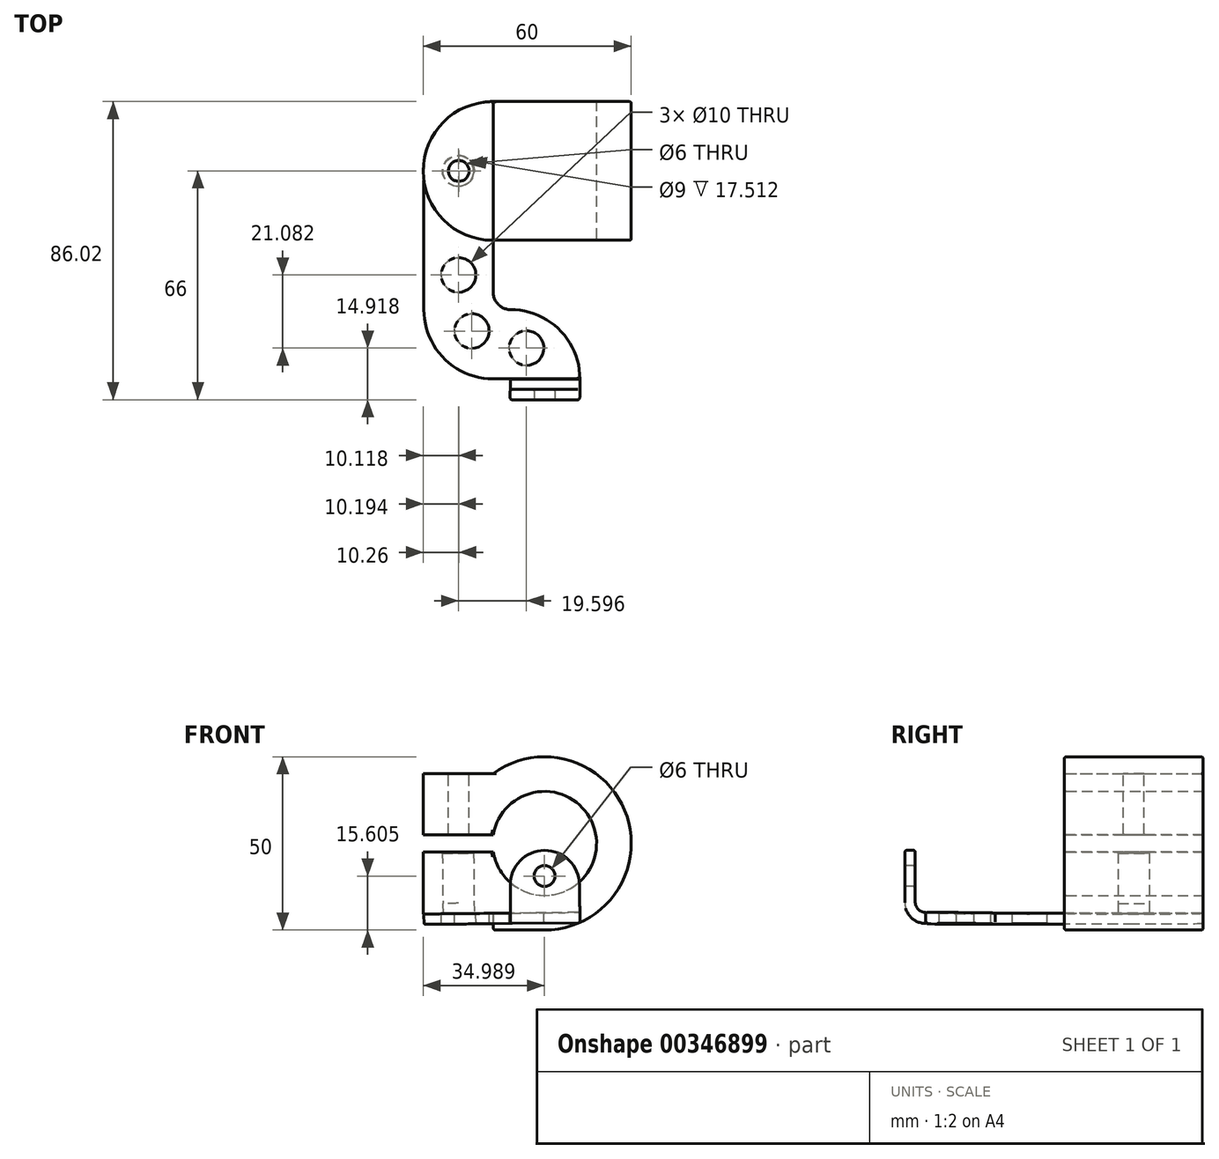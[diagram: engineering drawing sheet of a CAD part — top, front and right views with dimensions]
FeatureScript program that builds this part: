
annotation { "Feature Type Name" : "Feature", "Feature Type Description" : "" }
export const myFeature = defineFeature(function(context is Context, id is Id, definition is map)
    precondition{}
    {
        {
            var Q0;
            Q0=qCreatedBy(makeId("Front.planeOp"),FACE);
            var sketch = newSketch(context, id + "F0", { "sketchPlane" : qUnion([Q0])});
            skLineSegment(sketch, "E0.right", {"start": v(30, 0.21) * mm, "end": v(30, 0.21) * mm});
            skArc(sketch, "E1", {"start": v(-9.8, -2.5) * mm, "mid": v(20, 0) * mm, "end": v(-9.8, 2.5) * mm});
            skArc(sketch, "E2.filletArc", {"start": v(30, 0.21) * mm, "mid": v(16.2, 22.35) * mm, "end": v(-9.8, 20.16) * mm});
            skArc(sketch, "E3.filletArc", {"start": v(5, -25) * mm, "mid": v(22.75, -17.6) * mm, "end": v(30, 0.21) * mm});
            skLineSegment(sketch, "E4", {"start": v(-30, -2.5) * mm, "end": v(-9.8, -2.5) * mm});
            skLineSegment(sketch, "E5", {"start": v(-30, 2.5) * mm, "end": v(-9.8, 2.5) * mm});
            skLineSegment(sketch, "E6", {"start": v(-9.8, 20.16) * mm, "end": v(-30, 20.16) * mm});
            skLineSegment(sketch, "E7", {"start": v(-30, 20.16) * mm, "end": v(-30, 2.5) * mm});
            skLineSegment(sketch, "E8", {"start": v(-9.8, -20.16) * mm, "end": v(-9.74, -25) * mm});
            skLineSegment(sketch, "E9", {"start": v(-9.8, -20.16) * mm, "end": v(-30, -20.37) * mm});
            skLineSegment(sketch, "E10", {"start": v(-30, -2.5) * mm, "end": v(-30, -20.37) * mm});
            skLineSegment(sketch, "E11", {"start": v(-9.74, -25) * mm, "end": v(5, -25) * mm});
            skSolve(sketch);
        }
        {
            var Q0;
            Q0 = qSketchRegion(id + "F0", true);
            extrude(context, id + "F1", {"entities" : qUnion([Q0]), "endBound" : BoundingType.SYMMETRIC, "depth" : 40 * mm});
        }
        {
            var Q0;
            Q0=makeQuery(id+"F1.opExtrude","SWEPT_FACE",FACE,{"disambiguationData":[OSD([sQuery(id+"F0.wireOp",EDGE,"E6")])]});
            var sketch = newSketch(context, id + "F2", { "sketchPlane" : qUnion([Q0])});
            skCircle(sketch, "E12", {"center": v(-19.74, 0) * mm, "radius": 3 * mm});
            skSolve(sketch);
        }
        {
            var Q0;
            Q0 = qSketchRegion(id + "F2", true);
            extrude(context, id + "F3", {"entities" : qUnion([Q0]), "operationType" : NewBodyOperationType.REMOVE, "oppositeDirection" : true, "depth" : 50 * mm});
        }
        {
            var Q0;
            Q0=makeQuery(id+"F1.opExtrude","SWEPT_FACE",FACE,{"disambiguationData":[OSD([sQuery(id+"F0.wireOp",EDGE,"E9")])]});
            var sketch = newSketch(context, id + "F4", { "sketchPlane" : qUnion([Q0])});
            skCircle(sketch, "E13", {"center": v(-20, 0) * mm, "radius": 4.5 * mm});
            skSolve(sketch);
        }
        {
            var Q0;
            Q0 = qSketchRegion(id + "F4", true);
            extrude(context, id + "F5", {"entities" : qUnion([Q0]), "operationType" : NewBodyOperationType.REMOVE, "oppositeDirection" : true, "depth" : 18 * mm});
        }
        {
            var Q0;
            Q0=makeQuery(id+"F1.opExtrude","CAP_EDGE",EDGE,{"disambiguationData":[OSD([sQuery(id+"F0.wireOp",EDGE,"KFdVerdW-mngw-Xv3d-Wjoe-0c56VN0OnCSq")])],"isStart":true});
            var Q1;
            Q1=makeQuery(id+"F1.opExtrude","CAP_EDGE",EDGE,{"disambiguationData":[OSD([sQuery(id+"F0.wireOp",EDGE,"E7")])],"isStart":true});
            var Q2;
            Q2=makeQuery(id+"F1.opExtrude","CAP_EDGE",EDGE,{"disambiguationData":[OSD([sQuery(id+"F0.wireOp",EDGE,"KFdVerdW-mngw-Xv3d-Wjoe-0c56VN0OnCSq")])],"isStart":false});
            var Q3;
            Q3=makeQuery(id+"F1.opExtrude","CAP_EDGE",EDGE,{"disambiguationData":[OSD([sQuery(id+"F0.wireOp",EDGE,"E7")])],"isStart":false});
            var Q4;
            Q4=makeQuery(id+"F1.opExtrude","CAP_EDGE",EDGE,{"disambiguationData":[OSD([sQuery(id+"F0.wireOp",EDGE,"E10")])],"isStart":false});
            var Q5;
            Q5=makeQuery(id+"F1.opExtrude","CAP_EDGE",EDGE,{"disambiguationData":[OSD([sQuery(id+"F0.wireOp",EDGE,"E10")])],"isStart":true});
            fillet(context, id + "F6", {"entities" : qUnion([Q0, Q1, Q2, Q3, Q4, Q5]), "radius" : 20 * mm, "tangentPropagation" : true, "allowEdgeOverflow" : false});
        }
        {
            var Q0;
            Q0=makeQuery(id+"F1.opExtrude","CAP_EDGE",EDGE,{"disambiguationData":[OSD([sQuery(id+"F0.wireOp",EDGE,"E2.filletArc"),sQuery(id+"F0.wireOp",EDGE,"E3.filletArc")])],"isStart":false});
            var Q1;
            Q1=makeQuery(id+"F1.opExtrude","CAP_EDGE",EDGE,{"disambiguationData":[OSD([sQuery(id+"F0.wireOp",EDGE,"E0.top")])],"isStart":false});
            var Q2;
            Q2=makeQuery(id+"F1.opExtrude","CAP_EDGE",EDGE,{"disambiguationData":[OSD([sQuery(id+"F0.wireOp",EDGE,"E2.filletArc"),sQuery(id+"F0.wireOp",EDGE,"E3.filletArc")])],"isStart":true});
            var Q3;
            Q3=makeQuery(id+"F1.opExtrude","CAP_EDGE",EDGE,{"disambiguationData":[OSD([sQuery(id+"F0.wireOp",EDGE,"E0.top")])],"isStart":true});
            var Q4;
            Q4=makeQuery(id+"F1.opExtrude","CAP_EDGE",EDGE,{"disambiguationData":[OSD([sQuery(id+"F0.wireOp",EDGE,"E1")])],"isStart":false});
            var Q5;
            Q5=makeQuery(id+"F1.opExtrude","CAP_EDGE",EDGE,{"disambiguationData":[OSD([sQuery(id+"F0.wireOp",EDGE,"E1")])],"isStart":true});
            var Q6;
            Q6=makeQuery(id+"F1.opExtrude","CAP_EDGE",EDGE,{"disambiguationData":[OSD([sQuery(id+"F0.wireOp",EDGE,"E8")])],"isStart":false});
            var Q7;
            Q7=makeQuery(id+"F1.opExtrude","CAP_EDGE",EDGE,{"disambiguationData":[OSD([sQuery(id+"F0.wireOp",EDGE,"E8")])],"isStart":true});
            var Q8;
            Q8=makeQuery(id+"F1.opExtrude","SWEPT_EDGE",EDGE,{"disambiguationData":[OSD([sQuery(id+"F0.wireOp",EDGE,"E8"),sQuery(id+"F0.wireOp",EDGE,"E11")])]});
            var Q9;
            Q9=makeQuery(id+"F6.opFillet","BLEND_EDGE",EDGE,{"blendedFrom":[makeQuery(id+"F1.opExtrude","CAP_EDGE",EDGE,{"disambiguationData":[OSD([sQuery(id+"F0.wireOp",EDGE,"E7")])],"isStart":false}),makeQuery(id+"F1.opExtrude","SWEPT_FACE",FACE,{"disambiguationData":[OSD([sQuery(id+"F0.wireOp",EDGE,"E5")])]})],"blendedInto":[makeQuery(id+"F1.opExtrude","SWEPT_FACE",FACE,{"disambiguationData":[OSD([sQuery(id+"F0.wireOp",EDGE,"E5")])]})]});
            var Q10;
            Q10=makeQuery(id+"F6.opFillet","BLEND_EDGE",EDGE,{"blendedFrom":[makeQuery(id+"F1.opExtrude","CAP_EDGE",EDGE,{"disambiguationData":[OSD([sQuery(id+"F0.wireOp",EDGE,"E7")])],"isStart":false}),makeQuery(id+"F1.opExtrude","SWEPT_FACE",FACE,{"disambiguationData":[OSD([sQuery(id+"F0.wireOp",EDGE,"E6")])]})],"blendedInto":[makeQuery(id+"F1.opExtrude","SWEPT_FACE",FACE,{"disambiguationData":[OSD([sQuery(id+"F0.wireOp",EDGE,"E6")])]})]});
            var Q11;
            Q11=makeQuery(id+"F6.opFillet","BLEND_EDGE",EDGE,{"blendedFrom":[makeQuery(id+"F1.opExtrude","CAP_EDGE",EDGE,{"disambiguationData":[OSD([sQuery(id+"F0.wireOp",EDGE,"E10")])],"isStart":false}),makeQuery(id+"F1.opExtrude","SWEPT_FACE",FACE,{"disambiguationData":[OSD([sQuery(id+"F0.wireOp",EDGE,"E4")])]})],"blendedInto":[makeQuery(id+"F1.opExtrude","SWEPT_FACE",FACE,{"disambiguationData":[OSD([sQuery(id+"F0.wireOp",EDGE,"E4")])]})]});
            var Q12;
            Q12=makeQuery(id+"F6.opFillet","BLEND_EDGE",EDGE,{"blendedFrom":[makeQuery(id+"F1.opExtrude","CAP_EDGE",EDGE,{"disambiguationData":[OSD([sQuery(id+"F0.wireOp",EDGE,"E10")])],"isStart":false}),makeQuery(id+"F1.opExtrude","SWEPT_FACE",FACE,{"disambiguationData":[OSD([sQuery(id+"F0.wireOp",EDGE,"E9")])]})],"blendedInto":[makeQuery(id+"F1.opExtrude","SWEPT_FACE",FACE,{"disambiguationData":[OSD([sQuery(id+"F0.wireOp",EDGE,"E9")])]})]});
            var Q13;
            Q13=makeQuery(id+"F1.opExtrude","CAP_EDGE",EDGE,{"disambiguationData":[OSD([sQuery(id+"F0.wireOp",EDGE,"E11")])],"isStart":false});
            var Q14;
            Q14=makeQuery(id+"F1.opExtrude","CAP_EDGE",EDGE,{"disambiguationData":[OSD([sQuery(id+"F0.wireOp",EDGE,"E11")])],"isStart":true});
            fillet(context, id + "F7", {"entities" : qUnion([Q0, Q1, Q2, Q3, Q4, Q5, Q6, Q7, Q8, Q9, Q10, Q11, Q12, Q13, Q14]), "radius" : 0.5 * mm, "tangentPropagation" : true, "allowEdgeOverflow" : false});
        }
        {
            var Q0;
            Q0=makeQuery(id+"F16.boolean.opBoolean","INTERSECT",EDGE,{"derivedFrom":[makeQuery(id+"F5.boolean.opBoolean","COPY",FACE,{"derivedFrom":makeQuery(id+"F5.opExtrude","SWEPT_FACE",FACE,{"disambiguationData":[OSD([sQuery(id+"F4.wireOp",EDGE,"E13")])]})}),makeQuery(id+"F16.opExtrude","CAP_FACE",FACE,{"disambiguationData":[OSD([sQuery(id+"F15.wireOp",EDGE,"E39")])],"isStart":false})]});
            var Q1;
            Q1=makeQuery(id+"F5.boolean.opBoolean","INTERSECT",EDGE,{"derivedFrom":[makeQuery(id+"F1.opExtrude","SWEPT_FACE",FACE,{"disambiguationData":[OSD([sQuery(id+"F0.wireOp",EDGE,"E4")])]}),makeQuery(id+"F5.opExtrude","SWEPT_FACE",FACE,{"disambiguationData":[OSD([sQuery(id+"F4.wireOp",EDGE,"E13")])]})]});
            var Q2;
            Q2=makeQuery(id+"F3.boolean.opBoolean","INTERSECT",EDGE,{"derivedFrom":[makeQuery(id+"F1.opExtrude","SWEPT_FACE",FACE,{"disambiguationData":[OSD([sQuery(id+"F0.wireOp",EDGE,"E5")])]}),makeQuery(id+"F3.opExtrude","SWEPT_FACE",FACE,{"disambiguationData":[OSD([sQuery(id+"F2.wireOp",EDGE,"E12")])]})]});
            var Q3;
            Q3=makeQuery(id+"F16.boolean.opBoolean","COPY",EDGE,{"derivedFrom":makeQuery(id+"F16.opExtrude","CAP_EDGE",EDGE,{"disambiguationData":[OSD([sQuery(id+"F15.wireOp",EDGE,"E39")])],"isStart":true})});
            var Q4;
            Q4=makeQuery(id+"F3.boolean.opBoolean","COPY",EDGE,{"derivedFrom":makeQuery(id+"F3.opExtrude","CAP_EDGE",EDGE,{"disambiguationData":[OSD([sQuery(id+"F2.wireOp",EDGE,"E12")])],"isStart":true})});
            var Q5;
            Q5=makeQuery(id+"F5.boolean.opBoolean","INTERSECT",EDGE,{"derivedFrom":[makeQuery(id+"F1.opExtrude","SWEPT_FACE",FACE,{"disambiguationData":[OSD([sQuery(id+"F0.wireOp",EDGE,"E5")])]}),makeQuery(id+"F5.opExtrude","SWEPT_FACE",FACE,{"disambiguationData":[OSD([sQuery(id+"F4.wireOp",EDGE,"E13")])]})]});
            var Q6;
            Q6=makeQuery(id+"F5.boolean.opBoolean","INTERSECT",EDGE,{"derivedFrom":[makeQuery(id+"F3.boolean.opBoolean","COPY",FACE,{"disambiguationData":[TD([makeQuery(id+"F1.opExtrude","SWEPT_FACE",FACE,{"disambiguationData":[OSD([sQuery(id+"F0.wireOp",EDGE,"E5")])]})])],"derivedFrom":makeQuery(id+"F3.opExtrude","SWEPT_FACE",FACE,{"disambiguationData":[OSD([sQuery(id+"F2.wireOp",EDGE,"E12")])]})}),makeQuery(id+"F5.opExtrude","CAP_FACE",FACE,{"disambiguationData":[OSD([sQuery(id+"F4.wireOp",EDGE,"E13")])],"isStart":false})]});
            fillet(context, id + "F8", {"entities" : qUnion([Q0, Q1, Q2, Q3, Q4, Q5, Q6]), "radius" : 0.3 * mm, "tangentPropagation" : true, "allowEdgeOverflow" : false});
        }
        {
            var Q0;
            Q0=makeQuery(id+"F4.imprint","IMPRINT",FACE,{"disambiguationData":[TD([[makeQuery(id+"F4.imprint","IMPRINT",EDGE,{"derivedFrom":sQuery(id+"F4.wireOp",EDGE,"E13")}),-1.0]])]});
            var sketch = newSketch(context, id + "F9", { "sketchPlane" : qUnion([Q0])});
            skLineSegment(sketch, "E14.bottom", {"start": v(-10.03, -20.02) * mm, "end": v(-10.03, -20.02) * mm});
            skPoint(sketch, "E15.visualSharp", {"position": v(-30.03, -20.02) * mm});
            skArc(sketch, "E15.filletArc", {"start": v(-30.03, -0.02) * mm, "mid": v(-24.17, -14.17) * mm, "end": v(-10.03, -20.02) * mm});
            skLineSegment(sketch, "E16", {"start": v(-10.03, -20.02) * mm, "end": v(-10.03, 20) * mm});
            skLineSegment(sketch, "E17.bottom", {"start": v(14.97, 60) * mm, "end": v(-5.03, 60) * mm});
            skLineSegment(sketch, "E17.left", {"start": v(14.97, 60) * mm, "end": v(14.97, 60) * mm});
            skPoint(sketch, "E17.middle", {"position": v(4.97, 50) * mm});
            skLineSegment(sketch, "E18", {"start": v(-30.03, -0.02) * mm, "end": v(-30.03, 20) * mm});
            skLineSegment(sketch, "E19", {"start": v(-5.03, 40) * mm, "end": v(-5.03, 40) * mm});
            skLineSegment(sketch, "E20", {"start": v(-10.03, 20) * mm, "end": v(-30.03, 20) * mm});
            skLineSegment(sketch, "E21", {"start": v(-10.03, 20) * mm, "end": v(-10.03, 35) * mm});
            skLineSegment(sketch, "E22", {"start": v(-30.03, 20) * mm, "end": v(-30.03, 40) * mm});
            skLineSegment(sketch, "E23", {"start": v(-10.03, 60) * mm, "end": v(-5.03, 60) * mm});
            skPoint(sketch, "E24.visualSharp", {"position": v(-30.03, 60) * mm});
            skArc(sketch, "E24.filletArc", {"start": v(-10.03, 60) * mm, "mid": v(-24.17, 54.14) * mm, "end": v(-30.03, 40) * mm});
            skArc(sketch, "E25.filletArc", {"start": v(-5.03, 40) * mm, "mid": v(-8.57, 38.54) * mm, "end": v(-10.03, 35) * mm});
            skPoint(sketch, "E26.visualSharp", {"position": v(14.97, 40) * mm});
            skArc(sketch, "E26.filletArc", {"start": v(-5.03, 40) * mm, "mid": v(9.1, 45.86) * mm, "end": v(14.97, 60) * mm});
            skCircle(sketch, "E27", {"center": v(-20.03, 30) * mm, "radius": 5 * mm});
            skPoint(sketch, "E27.centerSnap0", {"position": v(-30.03, 30) * mm});
            skPoint(sketch, "E27.centerSnap1", {"position": v(-20.03, 20) * mm});
            skCircle(sketch, "E28", {"center": v(-16.2, 46.18) * mm, "radius": 5 * mm});
            skCircle(sketch, "E29", {"center": v(-0.44, 51.08) * mm, "radius": 5 * mm});
            skSolve(sketch);
        }
        {
            var Q0;
            Q0 = qSketchRegion(id + "F9", true);
            extrude(context, id + "F10", {"entities" : qUnion([Q0]), "depth" : 3 * mm});
        }
        {
            var Q0;
            Q0=makeQuery(id+"F10.opExtrude","SWEPT_FACE",FACE,{"disambiguationData":[OSD([sQuery(id+"F9.wireOp",EDGE,"E16"),sQuery(id+"F9.wireOp",EDGE,"E21")])]});
            var sketch = newSketch(context, id + "F11", { "sketchPlane" : qUnion([Q0])});
            skLineSegment(sketch, "E30", {"start": v(-60, -20.05) * mm, "end": v(-59.97, -20.05) * mm});
            skLineSegment(sketch, "E31", {"start": v(-60, -23.05) * mm, "end": v(-60, -23.05) * mm});
            skArc(sketch, "E32.MirrorCS", {"start": v(-60, -23.05) * mm, "mid": v(-64.24, -21.3) * mm, "end": v(-66, -17.05) * mm});
            skArc(sketch, "E33.MirrorCS", {"start": v(-60.03, -20.05) * mm, "mid": v(-62.15, -19.17) * mm, "end": v(-63.03, -17.05) * mm});
            skLineSegment(sketch, "E34.MirrorCS", {"start": v(-63.03, -17.05) * mm, "end": v(-63.03, -2.05) * mm});
            skLineSegment(sketch, "E35.MirrorCS", {"start": v(-66, -2.05) * mm, "end": v(-66, -17.05) * mm});
            skLineSegment(sketch, "E36.MirrorCS", {"start": v(-63.03, -2.05) * mm, "end": v(-66, -2.05) * mm});
            skLineSegment(sketch, "E37", {"start": v(-60.03, -20.05) * mm, "end": v(-60, -23.05) * mm});
            skSolve(sketch);
        }
        {
            var Q0;
            Q0 = qSketchRegion(id + "F11", true);
            extrude(context, id + "F12", {"entities" : qUnion([Q0]), "operationType" : NewBodyOperationType.ADD, "depth" : 25 * mm, "hasSecondDirection" : true, "secondDirectionOppositeDirection" : false, "secondDirectionDepth" : 5 * mm});
        }
        {
            var Q0;
            Q0=makeQuery(id+"F12.opExtrude","SWEPT_FACE",FACE,{"disambiguationData":[OSD([sQuery(id+"F11.wireOp",EDGE,"E35.MirrorCS")])]});
            var sketch = newSketch(context, id + "F13", { "sketchPlane" : qUnion([Q0])});
            skCircle(sketch, "E38", {"center": v(4.99, -9.4) * mm, "radius": 3 * mm});
            skPoint(sketch, "E38.centerSnap0", {"position": v(15.07, -9.4) * mm});
            skPoint(sketch, "E38.centerSnap1", {"position": v(4.99, -2) * mm});
            skSolve(sketch);
        }
        {
            var Q0;
            Q0 = qSketchRegion(id + "F13", true);
            extrude(context, id + "F14", {"entities" : qUnion([Q0]), "operationType" : NewBodyOperationType.REMOVE, "oppositeDirection" : true, "depth" : 3 * mm});
        }
        {
            var Q0;
            Q0=makeQuery(id+"F1.opExtrude","SWEPT_FACE",FACE,{"disambiguationData":[OSD([sQuery(id+"F0.wireOp",EDGE,"E9")])]});
            var sketch = newSketch(context, id + "F15", { "sketchPlane" : qUnion([Q0])});
            skCircle(sketch, "E39", {"center": v(-20.03, 0) * mm, "radius": 4.5 * mm});
            skSolve(sketch);
        }
        {
            var Q0;
            Q0 = qSketchRegion(id + "F15", true);
            extrude(context, id + "F16", {"entities" : qUnion([Q0]), "operationType" : NewBodyOperationType.REMOVE, "oppositeDirection" : true, "depth" : 3 * mm});
        }
        {
            var Q0;
            Q0=makeQuery(id+"F10.opExtrude","CAP_EDGE",EDGE,{"disambiguationData":[OSD([sQuery(id+"F9.wireOp",EDGE,"E27")])],"isStart":true});
            var Q1;
            Q1=makeQuery(id+"F10.opExtrude","CAP_EDGE",EDGE,{"disambiguationData":[OSD([sQuery(id+"F9.wireOp",EDGE,"E28")])],"isStart":true});
            var Q2;
            Q2=makeQuery(id+"F10.opExtrude","CAP_EDGE",EDGE,{"disambiguationData":[OSD([sQuery(id+"F9.wireOp",EDGE,"E29")])],"isStart":true});
            var Q3;
            Q3=makeQuery(id+"F10.opExtrude","CAP_EDGE",EDGE,{"disambiguationData":[OSD([sQuery(id+"F9.wireOp",EDGE,"E27")])],"isStart":false});
            var Q4;
            Q4=makeQuery(id+"F10.opExtrude","CAP_EDGE",EDGE,{"disambiguationData":[OSD([sQuery(id+"F9.wireOp",EDGE,"E28")])],"isStart":false});
            var Q5;
            Q5=makeQuery(id+"F10.opExtrude","CAP_EDGE",EDGE,{"disambiguationData":[OSD([sQuery(id+"F9.wireOp",EDGE,"E29")])],"isStart":false});
            var Q6;
            Q6=makeQuery(id+"F16.boolean.opBoolean","COPY",EDGE,{"derivedFrom":makeQuery(id+"F16.opExtrude","CAP_EDGE",EDGE,{"disambiguationData":[OSD([sQuery(id+"F15.wireOp",EDGE,"E39")])],"isStart":true})});
            var Q7;
            Q7=makeQuery(id+"F10.opExtrude","CAP_EDGE",EDGE,{"disambiguationData":[OSD([sQuery(id+"F9.wireOp",EDGE,"E18"),sQuery(id+"F9.wireOp",EDGE,"E22")])],"isStart":true});
            var Q8;
            Q8=makeQuery(id+"F12.opExtrude","SWEPT_EDGE",EDGE,{"disambiguationData":[OSD([sQuery(id+"F11.wireOp",EDGE,"E34.MirrorCS"),sQuery(id+"F11.wireOp",EDGE,"E36.MirrorCS")])]});
            var Q9;
            Q9=makeQuery(id+"F10.opExtrude","CAP_EDGE",EDGE,{"disambiguationData":[OSD([sQuery(id+"F9.wireOp",EDGE,"E25.filletArc")])],"isStart":true});
            var Q10;
            Q10=makeQuery(id+"F10.opExtrude","CAP_EDGE",EDGE,{"disambiguationData":[OSD([sQuery(id+"F9.wireOp",EDGE,"E16"),sQuery(id+"F9.wireOp",EDGE,"E21")])],"isStart":true});
            var Q11;
            Q11=makeQuery(id+"F10.opExtrude","CAP_EDGE",EDGE,{"disambiguationData":[OSD([sQuery(id+"F9.wireOp",EDGE,"E18"),sQuery(id+"F9.wireOp",EDGE,"E22")])],"isStart":false});
            var Q12;
            Q12=makeQuery(id+"F10.opExtrude","CAP_EDGE",EDGE,{"disambiguationData":[OSD([sQuery(id+"F9.wireOp",EDGE,"E16"),sQuery(id+"F9.wireOp",EDGE,"E21")])],"isStart":false});
            var Q13;
            Q13=makeQuery(id+"F10.opExtrude","CAP_EDGE",EDGE,{"disambiguationData":[OSD([sQuery(id+"F9.wireOp",EDGE,"E15.filletArc")])],"isStart":false});
            var Q14;
            Q14=makeQuery(id+"F10.opExtrude","CAP_EDGE",EDGE,{"disambiguationData":[OSD([sQuery(id+"F9.wireOp",EDGE,"E15.filletArc")])],"isStart":true});
            var Q15;
            Q15=makeQuery(id+"F10.opExtrude","CAP_EDGE",EDGE,{"disambiguationData":[OSD([sQuery(id+"F9.wireOp",EDGE,"E25.filletArc")])],"isStart":false});
            var Q16;
            Q16=makeQuery(id+"F10.opExtrude","CAP_EDGE",EDGE,{"disambiguationData":[OSD([sQuery(id+"F9.wireOp",EDGE,"E26.filletArc")])],"isStart":true});
            var Q17;
            Q17=makeQuery(id+"F10.opExtrude","CAP_EDGE",EDGE,{"disambiguationData":[OSD([sQuery(id+"F9.wireOp",EDGE,"E26.filletArc")])],"isStart":false});
            var Q18;
            Q18=makeQuery(id+"F12.opExtrude","CAP_EDGE",EDGE,{"disambiguationData":[OSD([sQuery(id+"F11.wireOp",EDGE,"E34.MirrorCS")])],"isStart":false});
            var Q19;
            Q19=makeQuery(id+"F12.opExtrude","CAP_EDGE",EDGE,{"disambiguationData":[OSD([sQuery(id+"F11.wireOp",EDGE,"E33.MirrorCS")])],"isStart":false});
            var Q20;
            Q20=makeQuery(id+"F12.opExtrude","CAP_EDGE",EDGE,{"disambiguationData":[OSD([sQuery(id+"F11.wireOp",EDGE,"E32.MirrorCS")])],"isStart":false});
            var Q21;
            Q21=makeQuery(id+"F12.opExtrude","CAP_EDGE",EDGE,{"disambiguationData":[OSD([sQuery(id+"F11.wireOp",EDGE,"E35.MirrorCS")])],"isStart":false});
            var Q22;
            Q22=makeQuery(id+"F12.opExtrude","SWEPT_EDGE",EDGE,{"disambiguationData":[OSD([sQuery(id+"F11.wireOp",EDGE,"E35.MirrorCS"),sQuery(id+"F11.wireOp",EDGE,"E36.MirrorCS")])]});
            var Q23;
            Q23=makeQuery(id+"F12.opExtrude","CAP_EDGE",EDGE,{"disambiguationData":[OSD([sQuery(id+"F11.wireOp",EDGE,"E35.MirrorCS")])],"isStart":true});
            var Q24;
            Q24=makeQuery(id+"F12.opExtrude","CAP_EDGE",EDGE,{"disambiguationData":[OSD([sQuery(id+"F11.wireOp",EDGE,"E34.MirrorCS")])],"isStart":true});
            var Q25;
            Q25=makeQuery(id+"F12.opExtrude","CAP_EDGE",EDGE,{"disambiguationData":[OSD([sQuery(id+"F11.wireOp",EDGE,"E33.MirrorCS")])],"isStart":true});
            var Q26;
            Q26=makeQuery(id+"F12.opExtrude","CAP_EDGE",EDGE,{"disambiguationData":[OSD([sQuery(id+"F11.wireOp",EDGE,"E32.MirrorCS")])],"isStart":true});
            var Q27;
            Q27=makeQuery(id+"F10.opExtrude","CAP_EDGE",EDGE,{"disambiguationData":[OSD([sQuery(id+"F9.wireOp",EDGE,"E24.filletArc")])],"isStart":true});
            var Q28;
            Q28=makeQuery(id+"F10.opExtrude","CAP_EDGE",EDGE,{"disambiguationData":[OSD([sQuery(id+"F9.wireOp",EDGE,"E24.filletArc")])],"isStart":false});
            var Q29;
            Q29=makeQuery(id+"F14.boolean.opBoolean","COPY",EDGE,{"derivedFrom":makeQuery(id+"F14.opExtrude","CAP_EDGE",EDGE,{"disambiguationData":[OSD([sQuery(id+"F13.wireOp",EDGE,"E38")])],"isStart":true})});
            var Q30;
            Q30=makeQuery(id+"F14.boolean.opBoolean","INTERSECT",EDGE,{"derivedFrom":[makeQuery(id+"F12.opExtrude","SWEPT_FACE",FACE,{"disambiguationData":[OSD([sQuery(id+"F11.wireOp",EDGE,"E34.MirrorCS")])]}),makeQuery(id+"F14.opExtrude","SWEPT_FACE",FACE,{"disambiguationData":[OSD([sQuery(id+"F13.wireOp",EDGE,"E38")])]})]});
            fillet(context, id + "F17", {"entities" : qUnion([Q0, Q1, Q2, Q3, Q4, Q5, Q6, Q7, Q8, Q9, Q10, Q11, Q12, Q13, Q14, Q15, Q16, Q17, Q18, Q19, Q20, Q21, Q22, Q23, Q24, Q25, Q26, Q27, Q28, Q29, Q30]), "radius" : 0.5 * mm, "allowEdgeOverflow" : false});
        }
        {
            var Q0;
            Q0=makeQuery(id+"F12.opExtrude","CAP_EDGE",EDGE,{"disambiguationData":[OSD([sQuery(id+"F11.wireOp",EDGE,"E36.MirrorCS")])],"isStart":true});
            var Q1;
            Q1=makeQuery(id+"F12.opExtrude","CAP_EDGE",EDGE,{"disambiguationData":[OSD([sQuery(id+"F11.wireOp",EDGE,"E36.MirrorCS")])],"isStart":false});
            fillet(context, id + "F18", {"entities" : qUnion([Q0, Q1]), "radius" : 10 * mm, "tangentPropagation" : true, "allowEdgeOverflow" : false});
        }
    });
